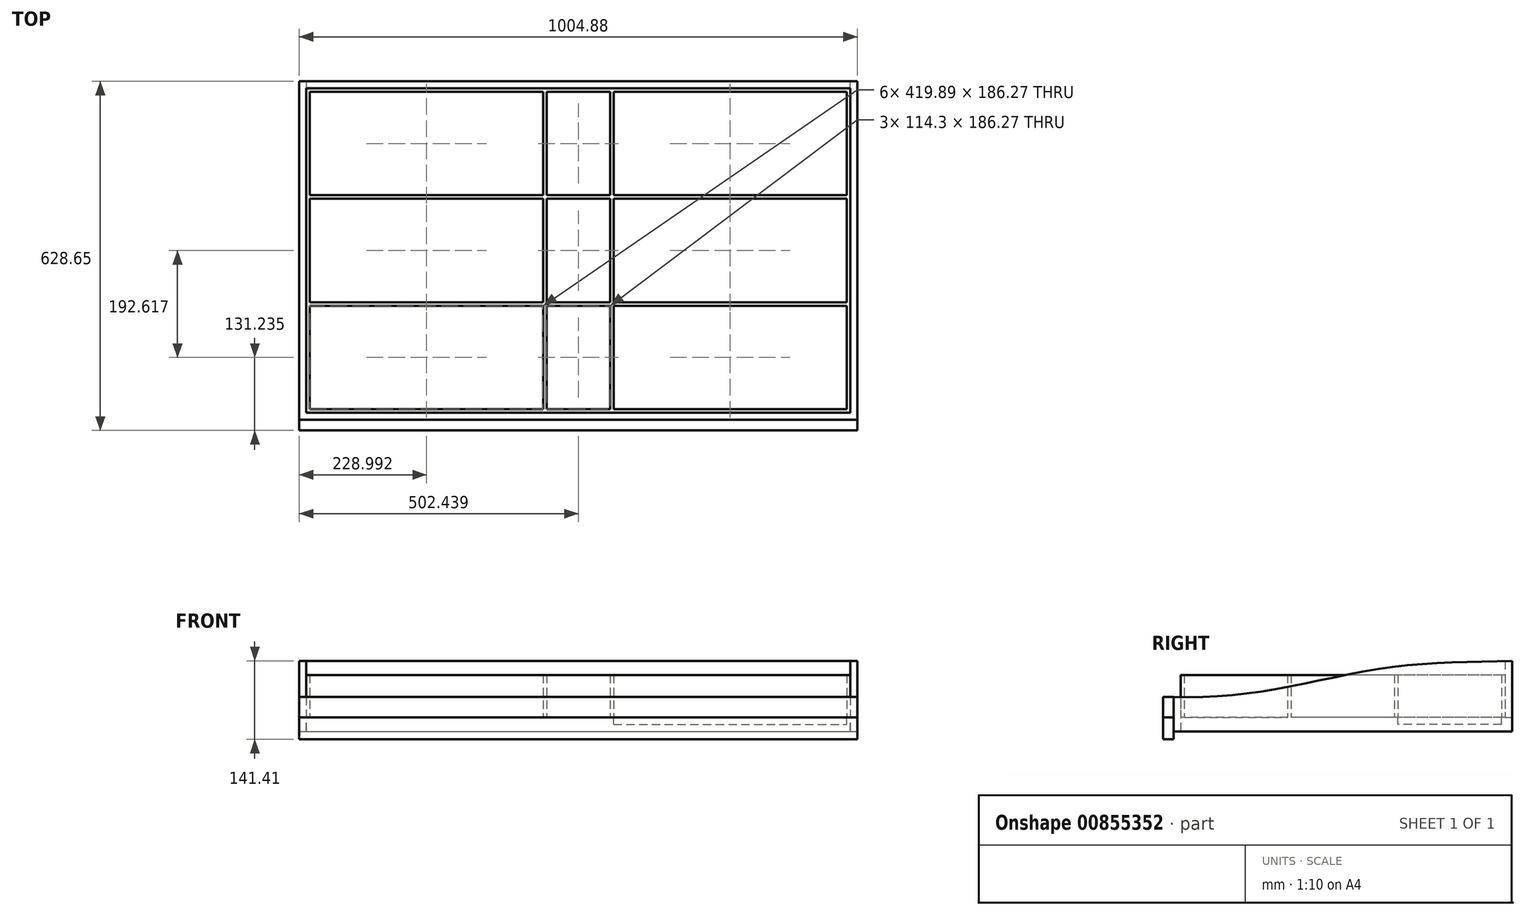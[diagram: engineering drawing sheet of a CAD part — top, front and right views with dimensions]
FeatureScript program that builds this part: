
annotation { "Feature Type Name" : "Feature", "Feature Type Description" : "" }
export const myFeature = defineFeature(function(context is Context, id is Id, definition is map)
    precondition{}
    {
        {
            var Q0;
            Q0=qCreatedBy(makeId("Top.planeOp"),FACE);
            var sketch = newSketch(context, id + "F0", { "sketchPlane" : qUnion([Q0])});
            skLineSegment(sketch, "E0.bottom", {"start": v(-26.7, 524.1) * mm, "end": v(978.2, 524.1) * mm});
            skLineSegment(sketch, "E0.top", {"start": v(-26.7, -85.5) * mm, "end": v(978.2, -85.5) * mm});
            skLineSegment(sketch, "E0.left", {"start": v(-26.7, 524.1) * mm, "end": v(-26.7, -85.5) * mm});
            skLineSegment(sketch, "E0.right", {"start": v(978.2, 524.1) * mm, "end": v(978.2, -85.5) * mm});
            skLineSegment(sketch, "E1.0", {"start": v(-14, 511.4) * mm, "end": v(965.5, 511.4) * mm});
            skLineSegment(sketch, "E1.1", {"start": v(-14, 511.4) * mm, "end": v(-14, -72.8) * mm});
            skLineSegment(sketch, "E1.2", {"start": v(-14, -72.8) * mm, "end": v(965.5, -72.8) * mm});
            skLineSegment(sketch, "E1.3", {"start": v(965.5, 511.4) * mm, "end": v(965.5, -72.8) * mm});
            skLineSegment(sketch, "E2.top", {"start": v(-26.7, -104.55) * mm, "end": v(978.2, -104.55) * mm});
            skLineSegment(sketch, "E2.left", {"start": v(-26.7, -85.5) * mm, "end": v(-26.7, -104.55) * mm});
            skLineSegment(sketch, "E2.right", {"start": v(978.2, -85.5) * mm, "end": v(978.2, -104.55) * mm});
            skLineSegment(sketch, "E3.0", {"start": v(-7.64, 505.05) * mm, "end": v(412.25, 505.05) * mm});
            skLineSegment(sketch, "E3.1", {"start": v(-7.64, 505.05) * mm, "end": v(-7.64, 318.78) * mm});
            skLineSegment(sketch, "E3.2", {"start": v(-7.64, -66.45) * mm, "end": v(412.25, -66.45) * mm});
            skLineSegment(sketch, "E3.3", {"start": v(959.14, 505.05) * mm, "end": v(959.14, 318.78) * mm});
            skLineSegment(sketch, "E4", {"start": v(-7.64, 126.17) * mm, "end": v(412.25, 126.17) * mm});
            skLineSegment(sketch, "E5", {"start": v(959.14, 312.43) * mm, "end": v(539.25, 312.43) * mm});
            skLineSegment(sketch, "E6.0", {"start": v(959.14, 318.78) * mm, "end": v(539.25, 318.78) * mm});
            skLineSegment(sketch, "E7.0", {"start": v(-7.64, 119.82) * mm, "end": v(412.25, 119.82) * mm});
            skLineSegment(sketch, "E8", {"start": v(412.25, -66.45) * mm, "end": v(412.25, 119.82) * mm});
            skLineSegment(sketch, "E9", {"start": v(412.25, 126.17) * mm, "end": v(412.25, 312.43) * mm});
            skLineSegment(sketch, "E10", {"start": v(412.25, 318.78) * mm, "end": v(412.25, 505.05) * mm});
            skLineSegment(sketch, "E11", {"start": v(532.9, 505.05) * mm, "end": v(532.9, 318.78) * mm});
            skLineSegment(sketch, "E12", {"start": v(532.9, 312.43) * mm, "end": v(532.9, 126.17) * mm});
            skLineSegment(sketch, "E13", {"start": v(532.9, 119.82) * mm, "end": v(532.9, -66.45) * mm});
            skLineSegment(sketch, "E14.0", {"start": v(418.6, 318.78) * mm, "end": v(418.6, 505.05) * mm});
            skLineSegment(sketch, "E15.0", {"start": v(418.6, 126.17) * mm, "end": v(418.6, 312.43) * mm});
            skLineSegment(sketch, "E16.0", {"start": v(418.6, -66.45) * mm, "end": v(418.6, 119.82) * mm});
            skLineSegment(sketch, "E17.0", {"start": v(539.25, 119.82) * mm, "end": v(539.25, -66.45) * mm});
            skLineSegment(sketch, "E18.trimOffspring", {"start": v(532.9, 318.78) * mm, "end": v(418.6, 318.78) * mm});
            skLineSegment(sketch, "E19.trimOffspring", {"start": v(532.9, 312.43) * mm, "end": v(418.6, 312.43) * mm});
            skLineSegment(sketch, "E20.trimOffspring", {"start": v(412.25, 318.78) * mm, "end": v(-7.64, 318.78) * mm});
            skLineSegment(sketch, "E21.trimOffspring", {"start": v(412.25, 312.43) * mm, "end": v(-7.64, 312.43) * mm});
            skLineSegment(sketch, "E22.trimOffspring", {"start": v(539.25, 126.17) * mm, "end": v(959.14, 126.17) * mm});
            skLineSegment(sketch, "E23.trimOffspring", {"start": v(539.25, 119.82) * mm, "end": v(959.14, 119.82) * mm});
            skLineSegment(sketch, "E24.trimOffspring", {"start": v(418.6, 126.17) * mm, "end": v(532.9, 126.17) * mm});
            skLineSegment(sketch, "E25.trimOffspring", {"start": v(418.6, 119.82) * mm, "end": v(532.9, 119.82) * mm});
            skLineSegment(sketch, "E26.trimOffspring", {"start": v(418.6, -66.45) * mm, "end": v(532.9, -66.45) * mm});
            skLineSegment(sketch, "E27.trimOffspring", {"start": v(539.25, -66.45) * mm, "end": v(959.14, -66.45) * mm});
            skLineSegment(sketch, "E28.trimOffspring", {"start": v(959.14, 312.43) * mm, "end": v(959.14, 126.17) * mm});
            skLineSegment(sketch, "E29.trimOffspring", {"start": v(959.14, 119.82) * mm, "end": v(959.14, -66.45) * mm});
            skLineSegment(sketch, "E30.trimOffspring", {"start": v(-7.64, 119.82) * mm, "end": v(-7.64, -66.45) * mm});
            skLineSegment(sketch, "E31.trimOffspring", {"start": v(-7.64, 312.43) * mm, "end": v(-7.64, 126.17) * mm});
            skLineSegment(sketch, "E32.0", {"start": v(532.9, 293.24) * mm, "end": v(532.9, 126.17) * mm});
            skLineSegment(sketch, "E33.0", {"start": v(539.25, 312.43) * mm, "end": v(539.25, 126.17) * mm});
            skLineSegment(sketch, "E34.0", {"start": v(539.25, 505.05) * mm, "end": v(539.25, 318.78) * mm});
            skLineSegment(sketch, "E35.trimOffspring", {"start": v(539.25, 505.05) * mm, "end": v(959.14, 505.05) * mm});
            skLineSegment(sketch, "E36.trimOffspring", {"start": v(418.6, 505.05) * mm, "end": v(532.9, 505.05) * mm});
            skLineSegment(sketch, "E37", {"start": v(965.5, 511.4) * mm, "end": v(965.5, 524.1) * mm});
            skLineSegment(sketch, "E38", {"start": v(-14, 511.4) * mm, "end": v(-14, 524.1) * mm});
            skSolve(sketch);
        }
        {
            var Q0;
            Q0=makeQuery(id+"F0.imprint","IMPRINT",FACE,{"disambiguationData":[TD([[makeQuery(id+"F0.imprint","IMPRINT",EDGE,{"derivedFrom":sQuery(id+"F0.wireOp",EDGE,"E0.bottom")}),-1.0]])]});
            var Q1;
            Q1=makeQuery(id+"F0.imprint","IMPRINT",FACE,{"disambiguationData":[TD([[makeQuery(id+"F0.imprint","IMPRINT",EDGE,{"derivedFrom":sQuery(id+"F0.wireOp",EDGE,"E1.0")}),1.0]])]});
            extrude(context, id + "F1", {"entities" : qUnion([Q0, Q1]), "depth" : 101.6 * mm, "offsetDistance" : 25.4 * mm});
        }
        {
            var Q0;
            Q0=makeQuery(id+"F0.imprint","IMPRINT",FACE,{"disambiguationData":[TD([[makeQuery(id+"F0.imprint","IMPRINT",EDGE,{"derivedFrom":sQuery(id+"F0.wireOp",EDGE,"E0.top")}),1.0]])]});
            extrude(context, id + "F2", {"entities" : qUnion([Q0]), "operationType" : NewBodyOperationType.ADD, "oppositeDirection" : true, "depth" : 25.4 * mm, "offsetDistance" : 25.4 * mm});
        }
        {
            var Q0;
            Q0=makeQuery(id+"F0.imprint","IMPRINT",FACE,{"disambiguationData":[TD([[makeQuery(id+"F0.imprint","IMPRINT",EDGE,{"derivedFrom":sQuery(id+"F0.wireOp",EDGE,"E3.3")}),-1.0]])]});
            var sketch = newSketch(context, id + "F3", { "sketchPlane" : qUnion([Q0])});
            skLineSegment(sketch, "E39.0", {"start": v(-26.7, 524.1) * mm, "end": v(-26.7, -85.5) * mm});
            skLineSegment(sketch, "E40.0", {"start": v(-26.7, -85.5) * mm, "end": v(978.2, -85.5) * mm});
            skLineSegment(sketch, "E41.0", {"start": v(978.2, 524.1) * mm, "end": v(978.2, -85.5) * mm});
            skLineSegment(sketch, "E42.0", {"start": v(-26.7, 524.1) * mm, "end": v(978.2, 524.1) * mm});
            skLineSegment(sketch, "E43.left", {"start": v(-26.7, -85.5) * mm, "end": v(-26.7, 524.1) * mm});
            skLineSegment(sketch, "E43.right", {"start": v(978.2, -85.5) * mm, "end": v(978.2, 524.1) * mm});
            skSolve(sketch);
        }
        {
            var Q0;
            Q0=makeQuery(id+"F3.imprint","IMPRINT",FACE,{"disambiguationData":[TD([[makeQuery(id+"F3.imprint","IMPRINT",EDGE,{"derivedFrom":sQuery(id+"F3.wireOp",EDGE,"E40.0")}),1.0]])]});
            var Q1;
            Q1=makeQuery(id+"F3.imprint","IMPRINT",FACE,{"disambiguationData":[TD([[makeQuery(id+"F3.imprint","IMPRINT",EDGE,{"derivedFrom":makeQuery(id+"F0.imprint","IMPRINT",EDGE,{"derivedFrom":sQuery(id+"F0.wireOp",EDGE,"E3.3")})}),-1.0]])]});
            extrude(context, id + "F4", {"entities" : qUnion([Q0, Q1]), "operationType" : NewBodyOperationType.ADD, "oppositeDirection" : true, "depth" : 12.7 * mm, "offsetDistance" : 25.4 * mm});
        }
        {
            var Q0;
            {var subQ0=sQuery(id+"F0.wireOp",EDGE,"E0.left");Q0=makeQuery(id+"F2.boolean.opBoolean","MERGE",FACE,{"derivedFrom":[makeQuery(id+"F1.opExtrude","SWEPT_FACE",FACE,{"disambiguationData":[OSD([subQ0])]}),makeQuery(id+"F2.opExtrude","SWEPT_FACE",FACE,{"disambiguationData":[OSD([subQ0])]})]});}
            var sketch = newSketch(context, id + "F5", { "sketchPlane" : qUnion([Q0])});
            skFitSpline(sketch, "E44", {"points": [v(-524.1, 101.6) * mm, v(-316.27, 91.73) * mm, v(-113.67, 53.29) * mm, v(85.5, 36.51) * mm], "startDerivative": vector(622.37, -26.3) * mm, "endDerivative": vector(608.29, 23.06) * mm});
            skLineSegment(sketch, "E45", {"start": v(-524.1, 101.6) * mm, "end": v(85.5, 101.6) * mm});
            skLineSegment(sketch, "E46", {"start": v(85.5, 101.6) * mm, "end": v(85.5, 36.51) * mm});
            skSolve(sketch);
        }
        {
            var Q0;
            Q0=makeQuery(id+"F5.imprint","IMPRINT",FACE,{"disambiguationData":[TD([[makeQuery(id+"F5.imprint","IMPRINT",EDGE,{"derivedFrom":sQuery(id+"F5.wireOp",EDGE,"E44")}),1.0]])]});
            extrude(context, id + "F6", {"entities" : qUnion([Q0]), "operationType" : NewBodyOperationType.REMOVE, "endBound" : BoundingType.THROUGH_ALL, "oppositeDirection" : true, "depth" : 25.4 * mm, "offsetDistance" : 25.4 * mm});
        }
        {
            var Q0;
            Q0=makeQuery(id+"F0.imprint","IMPRINT",FACE,{"disambiguationData":[TD([[makeQuery(id+"F0.imprint","IMPRINT",EDGE,{"derivedFrom":sQuery(id+"F0.wireOp",EDGE,"E0.top")}),-1.0]])]});
            extrude(context, id + "F7", {"entities" : qUnion([Q0]), "depth" : 36.5 * mm, "offsetDistance" : 25.4 * mm});
        }
        {
            var Q0;
            Q0=makeQuery(id+"F0.imprint","IMPRINT",FACE,{"disambiguationData":[TD([[makeQuery(id+"F0.imprint","IMPRINT",EDGE,{"derivedFrom":sQuery(id+"F0.wireOp",EDGE,"E0.top")}),-1.0]])]});
            extrude(context, id + "F8", {"entities" : qUnion([Q0]), "oppositeDirection" : true, "depth" : 39.81 * mm, "offsetDistance" : 25.4 * mm});
        }
        {
            var Q0;
            Q0=makeQuery(id+"F0.imprint","IMPRINT",FACE,{"disambiguationData":[TD([[makeQuery(id+"F0.imprint","IMPRINT",EDGE,{"derivedFrom":sQuery(id+"F0.wireOp",EDGE,"E1.0")}),-1.0]])]});
            extrude(context, id + "F9", {"entities" : qUnion([Q0]), "depth" : 76.2 * mm, "offsetDistance" : 25.4 * mm});
        }
    });
